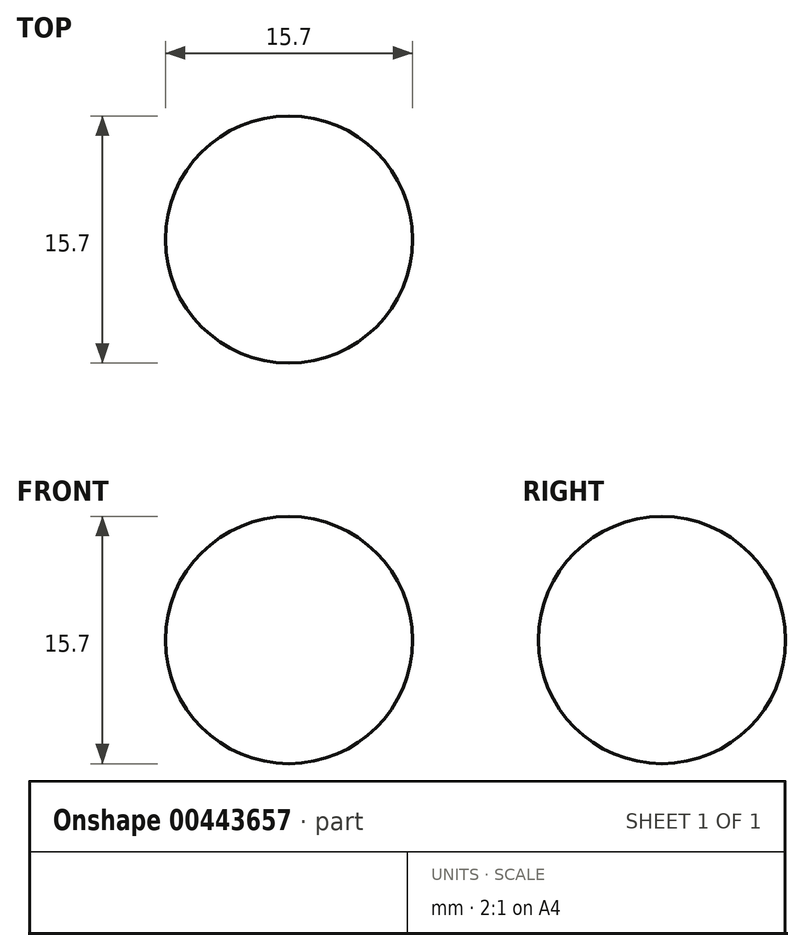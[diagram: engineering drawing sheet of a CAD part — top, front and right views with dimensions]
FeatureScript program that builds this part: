
annotation { "Feature Type Name" : "Feature", "Feature Type Description" : "" }
export const myFeature = defineFeature(function(context is Context, id is Id, definition is map)
    precondition{}
    {
        {
            var Q0;
            Q0=qCreatedBy(makeId("Top.planeOp"),FACE);
            var sketch = newSketch(context, id + "F0", { "sketchPlane" : qUnion([Q0])});
            skArc(sketch, "E0", {"start": v(0, -7.85) * mm, "mid": v(7.85, 0) * mm, "end": v(0, 7.85) * mm});
            skLineSegment(sketch, "E1", {"start": v(0, 7.85) * mm, "end": v(0, -7.85) * mm});
            skSolve(sketch);
        }
        {
            var Q0;
            Q0=makeQuery(id+"F0.imprint","IMPRINT",FACE,{"disambiguationData":[TD([[makeQuery(id+"F0.imprint","IMPRINT",EDGE,{"derivedFrom":sQuery(id+"F0.wireOp",EDGE,"E0")}),1.0]])]});
            var Q1;
            Q1=sQuery(id+"F0.wireOp",EDGE,"E1");
            revolve(context, id + "F1", {"entities" : qUnion([Q0]), "axis" : qUnion([Q1]), "revolveType" : RevolveType.FULL});
        }
    });
